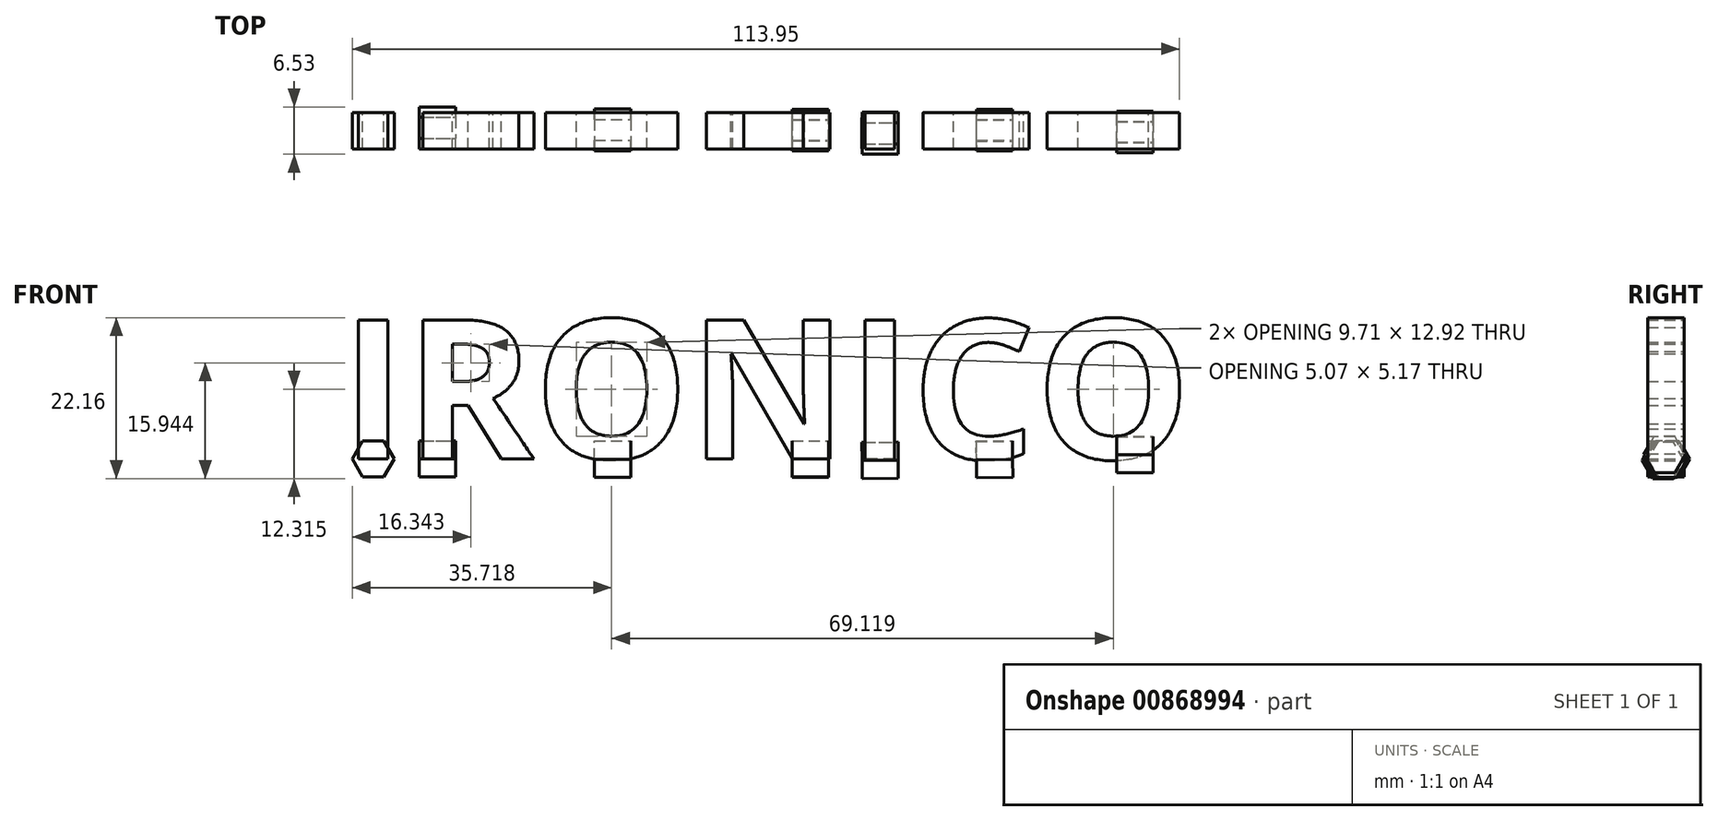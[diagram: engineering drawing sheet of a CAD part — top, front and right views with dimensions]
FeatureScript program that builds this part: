
annotation { "Feature Type Name" : "Feature", "Feature Type Description" : "" }
export const myFeature = defineFeature(function(context is Context, id is Id, definition is map)
    precondition{}
    {
        {
            var Q0;
            Q0=qCreatedBy(makeId("Front.planeOp"),FACE);
            var sketch = newSketch(context, id + "F0", { "sketchPlane" : qUnion([Q0])});
            skText(sketch, "E0", { "text": "IRONICO\n", "fontName": "OpenSans-Bold.ttf"});
            const initialGuessF0  = {"E0": [-0.04507, 0, 1, 0, 0.01931]};
            skSetInitialGuess(sketch, initialGuessF0);
            skSolve(sketch);
        }
        {
            var Q0;
            Q0 = qSketchRegion(id + "F0", true);
            extrude(context, id + "F1", {"entities" : qUnion([Q0]), "depth" : 5 * mm, "offsetDistance" : 25 * mm});
        }
        {
            var Q0;
            Q0=qCreatedBy(makeId("Front.planeOp"),FACE);
            var sketch = newSketch(context, id + "F2", { "sketchPlane" : qUnion([Q0])});
            skCircle(sketch, "E1.cCircle", {"center": v(-40.65, 0) * mm, "radius": 2.5 * mm, "construction": true});
            skLineSegment(sketch, "E1.0", {"start": v(-37.76, 0) * mm, "end": v(-39.2, -2.5) * mm});
            skLineSegment(sketch, "E1.1", {"start": v(-39.2, -2.5) * mm, "end": v(-42.09, -2.5) * mm});
            skLineSegment(sketch, "E1.2", {"start": v(-42.09, -2.5) * mm, "end": v(-43.53, 0) * mm});
            skLineSegment(sketch, "E1.3", {"start": v(-43.53, 0) * mm, "end": v(-42.09, 2.5) * mm});
            skLineSegment(sketch, "E1.4", {"start": v(-42.09, 2.5) * mm, "end": v(-39.2, 2.5) * mm});
            skLineSegment(sketch, "E1.5", {"start": v(-39.2, 2.5) * mm, "end": v(-37.76, 0) * mm});
            skPoint(sketch, "E1.0.midPoint", {"position": v(-38.48, -1.25) * mm});
            skCircle(sketch, "E2.cCircle", {"center": v(-31.74, 0) * mm, "radius": 2.5 * mm, "construction": true});
            skLineSegment(sketch, "E2.0", {"start": v(-28.85, 0) * mm, "end": v(-30.3, -2.5) * mm});
            skLineSegment(sketch, "E2.1", {"start": v(-30.3, -2.5) * mm, "end": v(-33.18, -2.5) * mm});
            skLineSegment(sketch, "E2.2", {"start": v(-33.18, -2.5) * mm, "end": v(-34.62, 0) * mm});
            skLineSegment(sketch, "E2.3", {"start": v(-34.62, 0) * mm, "end": v(-33.18, 2.5) * mm});
            skLineSegment(sketch, "E2.4", {"start": v(-33.18, 2.5) * mm, "end": v(-30.3, 2.5) * mm});
            skLineSegment(sketch, "E2.5", {"start": v(-30.3, 2.5) * mm, "end": v(-28.85, 0) * mm});
            skPoint(sketch, "E2.0.midPoint", {"position": v(-29.57, -1.25) * mm});
            skCircle(sketch, "E3.cCircle", {"center": v(-7.76, 0) * mm, "radius": 2.5 * mm, "construction": true});
            skLineSegment(sketch, "E3.0", {"start": v(-4.87, 0) * mm, "end": v(-6.31, -2.5) * mm});
            skLineSegment(sketch, "E3.1", {"start": v(-6.31, -2.5) * mm, "end": v(-9.2, -2.5) * mm});
            skLineSegment(sketch, "E3.2", {"start": v(-9.2, -2.5) * mm, "end": v(-10.64, 0) * mm});
            skLineSegment(sketch, "E3.3", {"start": v(-10.64, 0) * mm, "end": v(-9.2, 2.5) * mm});
            skLineSegment(sketch, "E3.4", {"start": v(-9.2, 2.5) * mm, "end": v(-6.31, 2.5) * mm});
            skLineSegment(sketch, "E3.5", {"start": v(-6.31, 2.5) * mm, "end": v(-4.87, 0) * mm});
            skPoint(sketch, "E3.0.midPoint", {"position": v(-5.6, -1.25) * mm});
            skCircle(sketch, "E4.cCircle", {"center": v(7.09, 0) * mm, "radius": 2.5 * mm, "construction": true});
            skLineSegment(sketch, "E4.0", {"start": v(9.98, 0.02) * mm, "end": v(8.55, -2.49) * mm});
            skLineSegment(sketch, "E4.1", {"start": v(8.55, -2.49) * mm, "end": v(5.66, -2.51) * mm});
            skLineSegment(sketch, "E4.2", {"start": v(5.66, -2.51) * mm, "end": v(4.2, -0.02) * mm});
            skLineSegment(sketch, "E4.3", {"start": v(4.2, -0.02) * mm, "end": v(5.63, 2.49) * mm});
            skLineSegment(sketch, "E4.4", {"start": v(5.63, 2.49) * mm, "end": v(8.51, 2.51) * mm});
            skLineSegment(sketch, "E4.5", {"start": v(8.51, 2.51) * mm, "end": v(9.98, 0.02) * mm});
            skPoint(sketch, "E4.0.midPoint", {"position": v(9.26, -1.23) * mm});
            skCircle(sketch, "E5.cCircle", {"center": v(29.25, 0) * mm, "radius": 2.5 * mm, "construction": true});
            skLineSegment(sketch, "E5.0", {"start": v(32.14, 0.02) * mm, "end": v(30.72, -2.49) * mm});
            skLineSegment(sketch, "E5.1", {"start": v(30.72, -2.49) * mm, "end": v(27.83, -2.51) * mm});
            skLineSegment(sketch, "E5.2", {"start": v(27.83, -2.51) * mm, "end": v(26.37, -0.02) * mm});
            skLineSegment(sketch, "E5.3", {"start": v(26.37, -0.02) * mm, "end": v(27.8, 2.49) * mm});
            skLineSegment(sketch, "E5.4", {"start": v(27.8, 2.49) * mm, "end": v(30.68, 2.51) * mm});
            skLineSegment(sketch, "E5.5", {"start": v(30.68, 2.51) * mm, "end": v(32.14, 0.02) * mm});
            skPoint(sketch, "E5.0.midPoint", {"position": v(31.43, -1.23) * mm});
            skCircle(sketch, "E6.cCircle", {"center": v(44.36, -0.36) * mm, "radius": 2.5 * mm, "construction": true});
            skLineSegment(sketch, "E6.0", {"start": v(47.24, -0.4) * mm, "end": v(45.77, -2.88) * mm});
            skLineSegment(sketch, "E6.1", {"start": v(45.77, -2.88) * mm, "end": v(42.88, -2.85) * mm});
            skLineSegment(sketch, "E6.2", {"start": v(42.88, -2.85) * mm, "end": v(41.47, -0.33) * mm});
            skLineSegment(sketch, "E6.3", {"start": v(41.47, -0.33) * mm, "end": v(42.94, 2.15) * mm});
            skLineSegment(sketch, "E6.4", {"start": v(42.94, 2.15) * mm, "end": v(45.83, 2.12) * mm});
            skLineSegment(sketch, "E6.5", {"start": v(45.83, 2.12) * mm, "end": v(47.24, -0.4) * mm});
            skPoint(sketch, "E6.0.midPoint", {"position": v(46.5, -1.64) * mm});
            skCircle(sketch, "E7.cCircle", {"center": v(61.76, 0) * mm, "radius": 2.5 * mm, "construction": true});
            skLineSegment(sketch, "E7.0", {"start": v(64.65, -0.03) * mm, "end": v(63.18, -2.51) * mm});
            skLineSegment(sketch, "E7.1", {"start": v(63.18, -2.51) * mm, "end": v(60.3, -2.49) * mm});
            skLineSegment(sketch, "E7.2", {"start": v(60.3, -2.49) * mm, "end": v(58.88, 0.03) * mm});
            skLineSegment(sketch, "E7.3", {"start": v(58.88, 0.03) * mm, "end": v(60.34, 2.51) * mm});
            skLineSegment(sketch, "E7.4", {"start": v(60.34, 2.51) * mm, "end": v(63.23, 2.49) * mm});
            skLineSegment(sketch, "E7.5", {"start": v(63.23, 2.49) * mm, "end": v(64.65, -0.03) * mm});
            skPoint(sketch, "E7.0.midPoint", {"position": v(63.92, -1.27) * mm});
            skLineSegment(sketch, "E8", {"start": v(-40.65, 2.5) * mm, "end": v(-40.65, -2.5) * mm});
            skLineSegment(sketch, "E9", {"start": v(-31.74, 2.5) * mm, "end": v(-31.74, -2.5) * mm});
            skLineSegment(sketch, "E10", {"start": v(-7.76, 2.5) * mm, "end": v(-7.76, -2.5) * mm});
            skLineSegment(sketch, "E11", {"start": v(7.07, 2.5) * mm, "end": v(7.07, -2.5) * mm});
            skLineSegment(sketch, "E12", {"start": v(29.24, 2.5) * mm, "end": v(29.25, -2.5) * mm});
            skLineSegment(sketch, "E13", {"start": v(44.39, 2.14) * mm, "end": v(44.42, -2.87) * mm});
            skLineSegment(sketch, "E14", {"start": v(61.79, 2.5) * mm, "end": v(61.79, -2.5) * mm});
            skSolve(sketch);
        }
        {
            var Q0;
            Q0 = qSketchRegion(id + "F2", true);
            extrude(context, id + "F3", {"entities" : qUnion([Q0]), "depth" : 5 * mm, "offsetDistance" : 25 * mm});
        }
        {
            var Q0;
            Q0=makeQuery(id+"F3.opExtrude","SWEPT_BODY",BODY,{"disambiguationData":[OSD([sQuery(id+"F2.wireOp",EDGE,"E1.0"),sQuery(id+"F2.wireOp",EDGE,"E1.1"),sQuery(id+"F2.wireOp",EDGE,"E1.2"),sQuery(id+"F2.wireOp",EDGE,"E1.3"),sQuery(id+"F2.wireOp",EDGE,"E1.4"),sQuery(id+"F2.wireOp",EDGE,"E1.5")])]});
            transform(context, id + "F4", {"entities" : qUnion([Q0]), "transformType" : TransformType.TRANSLATION_3D, "dx" : -2.8 * mm, "dy" : 2.6 * mm, "dz" : 0 * mm, "makeCopy" : false});
        }
        {
            var Q0;
            Q0=makeQuery(id+"F3.opExtrude","SWEPT_BODY",BODY,{"disambiguationData":[OSD([sQuery(id+"F2.wireOp",EDGE,"E1.0"),sQuery(id+"F2.wireOp",EDGE,"E1.1"),sQuery(id+"F2.wireOp",EDGE,"E1.2"),sQuery(id+"F2.wireOp",EDGE,"E1.3"),sQuery(id+"F2.wireOp",EDGE,"E1.4"),sQuery(id+"F2.wireOp",EDGE,"E1.5")])]});
            transform(context, id + "F5", {"entities" : qUnion([Q0]), "transformType" : TransformType.TRANSLATION_3D, "dx" : 2.8 * mm, "dy" : -2.6 * mm, "dz" : 0 * mm, "makeCopy" : false});
        }
        {
            var Q0;
            Q0=sQuery(id+"F2.wireOp",EDGE,"E14");
            var Q1;
            Q1=sQuery(id+"F2.wireOp",EDGE,"E13");
            var Q2;
            Q2=sQuery(id+"F2.wireOp",EDGE,"E12");
            var Q3;
            Q3=sQuery(id+"F2.wireOp",EDGE,"E11");
            var Q4;
            Q4=sQuery(id+"F2.wireOp",EDGE,"E8");
            var Q5;
            Q5=sQuery(id+"F2.wireOp",EDGE,"E9");
            var Q6;
            Q6=sQuery(id+"F2.wireOp",EDGE,"E10");
            extrude(context, id + "F6", {"bodyType" : ToolBodyType.SURFACE, "surfaceEntities" : qUnion([Q0, Q1, Q2, Q3, Q4, Q5, Q6]), "depth" : 5 * mm, "offsetDistance" : 25 * mm});
        }
        {
            var Q0;
            Q0=makeQuery(id+"F3.opExtrude","SWEPT_BODY",BODY,{"disambiguationData":[OSD([sQuery(id+"F2.wireOp",EDGE,"E2.0"),sQuery(id+"F2.wireOp",EDGE,"E2.1"),sQuery(id+"F2.wireOp",EDGE,"E2.2"),sQuery(id+"F2.wireOp",EDGE,"E2.3"),sQuery(id+"F2.wireOp",EDGE,"E2.4"),sQuery(id+"F2.wireOp",EDGE,"E2.5")])]});
            var Q1;
            Q1=makeQuery(id+"F6.opExtrude","SWEPT_BODY",BODY,{"disambiguationData":[OSD([sQuery(id+"F2.wireOp",EDGE,"E9")])]});
            var Q2;
            Q2=makeQuery(id+"F6.opExtrude","CAP_EDGE",EDGE,{"disambiguationData":[OSD([sQuery(id+"F2.wireOp",EDGE,"E9")])],"isStart":true});
            transform(context, id + "F7", {"entities" : qUnion([Q0, Q1]), "transformType" : TransformType.ROTATION, "transformAxis" : qUnion([Q2]), "angle" : 90 * degree, "makeCopy" : false});
        }
        {
            var Q0;
            Q0=makeQuery(id+"F3.opExtrude","SWEPT_BODY",BODY,{"disambiguationData":[OSD([sQuery(id+"F2.wireOp",EDGE,"E2.0"),sQuery(id+"F2.wireOp",EDGE,"E2.1"),sQuery(id+"F2.wireOp",EDGE,"E2.2"),sQuery(id+"F2.wireOp",EDGE,"E2.3"),sQuery(id+"F2.wireOp",EDGE,"E2.4"),sQuery(id+"F2.wireOp",EDGE,"E2.5")])]});
            var Q1;
            Q1=makeQuery(id+"F6.opExtrude","SWEPT_BODY",BODY,{"disambiguationData":[OSD([sQuery(id+"F2.wireOp",EDGE,"E9")])]});
            transform(context, id + "F8", {"entities" : qUnion([Q0, Q1]), "transformType" : TransformType.TRANSLATION_3D, "dx" : 2.44 * mm, "dy" : -2.1 * mm, "dz" : 0 * mm, "makeCopy" : false});
        }
        {
            var Q0;
            Q0=makeQuery(id+"F3.opExtrude","SWEPT_BODY",BODY,{"disambiguationData":[OSD([sQuery(id+"F2.wireOp",EDGE,"E3.0"),sQuery(id+"F2.wireOp",EDGE,"E3.1"),sQuery(id+"F2.wireOp",EDGE,"E3.2"),sQuery(id+"F2.wireOp",EDGE,"E3.3"),sQuery(id+"F2.wireOp",EDGE,"E3.4"),sQuery(id+"F2.wireOp",EDGE,"E3.5")])]});
            var Q1;
            Q1=makeQuery(id+"F6.opExtrude","SWEPT_BODY",BODY,{"disambiguationData":[OSD([sQuery(id+"F2.wireOp",EDGE,"E10")])]});
            var Q2;
            Q2=makeQuery(id+"F6.opExtrude","CAP_EDGE",EDGE,{"disambiguationData":[OSD([sQuery(id+"F2.wireOp",EDGE,"E10")])],"isStart":false});
            transform(context, id + "F9", {"entities" : qUnion([Q0, Q1]), "transformType" : TransformType.ROTATION, "transformAxis" : qUnion([Q2]), "angle" : 90 * degree, "makeCopy" : false});
        }
        {
            var Q0;
            Q0=makeQuery(id+"F3.opExtrude","SWEPT_BODY",BODY,{"disambiguationData":[OSD([sQuery(id+"F2.wireOp",EDGE,"E3.0"),sQuery(id+"F2.wireOp",EDGE,"E3.1"),sQuery(id+"F2.wireOp",EDGE,"E3.2"),sQuery(id+"F2.wireOp",EDGE,"E3.3"),sQuery(id+"F2.wireOp",EDGE,"E3.4"),sQuery(id+"F2.wireOp",EDGE,"E3.5")])]});
            var Q1;
            Q1=makeQuery(id+"F6.opExtrude","SWEPT_BODY",BODY,{"disambiguationData":[OSD([sQuery(id+"F2.wireOp",EDGE,"E10")])]});
            transform(context, id + "F10", {"entities" : qUnion([Q0, Q1]), "transformType" : TransformType.TRANSLATION_3D, "dx" : -2.4 * mm, "dy" : 2.6 * mm, "dz" : -0.05 * mm, "makeCopy" : false});
        }
        {
            var Q0;
            Q0=makeQuery(id+"F3.opExtrude","SWEPT_BODY",BODY,{"disambiguationData":[OSD([sQuery(id+"F2.wireOp",EDGE,"E4.0"),sQuery(id+"F2.wireOp",EDGE,"E4.1"),sQuery(id+"F2.wireOp",EDGE,"E4.2"),sQuery(id+"F2.wireOp",EDGE,"E4.3"),sQuery(id+"F2.wireOp",EDGE,"E4.4"),sQuery(id+"F2.wireOp",EDGE,"E4.5")])]});
            var Q1;
            Q1=makeQuery(id+"F6.opExtrude","SWEPT_BODY",BODY,{"disambiguationData":[OSD([sQuery(id+"F2.wireOp",EDGE,"E11")])]});
            var Q2;
            Q2=makeQuery(id+"F6.opExtrude","CAP_EDGE",EDGE,{"disambiguationData":[OSD([sQuery(id+"F2.wireOp",EDGE,"E11")])],"isStart":true});
            transform(context, id + "F11", {"entities" : qUnion([Q0, Q1]), "transformType" : TransformType.ROTATION, "transformAxis" : qUnion([Q2]), "angle" : 90 * degree, "makeCopy" : false});
        }
        {
            var Q0;
            Q0=makeQuery(id+"F3.opExtrude","SWEPT_BODY",BODY,{"disambiguationData":[OSD([sQuery(id+"F2.wireOp",EDGE,"E4.0"),sQuery(id+"F2.wireOp",EDGE,"E4.1"),sQuery(id+"F2.wireOp",EDGE,"E4.2"),sQuery(id+"F2.wireOp",EDGE,"E4.3"),sQuery(id+"F2.wireOp",EDGE,"E4.4"),sQuery(id+"F2.wireOp",EDGE,"E4.5")])]});
            var Q1;
            Q1=makeQuery(id+"F6.opExtrude","SWEPT_BODY",BODY,{"disambiguationData":[OSD([sQuery(id+"F2.wireOp",EDGE,"E11")])]});
            transform(context, id + "F12", {"entities" : qUnion([Q0, Q1]), "transformType" : TransformType.TRANSLATION_3D, "dx" : 15 * mm, "dy" : -2.4 * mm, "dz" : 0 * mm, "makeCopy" : false});
        }
        {
            var Q0;
            Q0=makeQuery(id+"F3.opExtrude","SWEPT_BODY",BODY,{"disambiguationData":[OSD([sQuery(id+"F2.wireOp",EDGE,"E5.0"),sQuery(id+"F2.wireOp",EDGE,"E5.1"),sQuery(id+"F2.wireOp",EDGE,"E5.2"),sQuery(id+"F2.wireOp",EDGE,"E5.3"),sQuery(id+"F2.wireOp",EDGE,"E5.4"),sQuery(id+"F2.wireOp",EDGE,"E5.5")])]});
            var Q1;
            Q1=makeQuery(id+"F6.opExtrude","SWEPT_BODY",BODY,{"disambiguationData":[OSD([sQuery(id+"F2.wireOp",EDGE,"E12")])]});
            var Q2;
            Q2=makeQuery(id+"F6.opExtrude","CAP_EDGE",EDGE,{"disambiguationData":[OSD([sQuery(id+"F2.wireOp",EDGE,"E12")])],"isStart":false});
            transform(context, id + "F13", {"entities" : qUnion([Q0, Q1]), "transformType" : TransformType.ROTATION, "transformAxis" : qUnion([Q2]), "angle" : 90 * degree, "makeCopy" : false});
        }
        {
            var Q0;
            Q0=makeQuery(id+"F6.opExtrude","SWEPT_BODY",BODY,{"disambiguationData":[OSD([sQuery(id+"F2.wireOp",EDGE,"E12")])]});
            var Q1;
            Q1=makeQuery(id+"F3.opExtrude","SWEPT_BODY",BODY,{"disambiguationData":[OSD([sQuery(id+"F2.wireOp",EDGE,"E5.0"),sQuery(id+"F2.wireOp",EDGE,"E5.1"),sQuery(id+"F2.wireOp",EDGE,"E5.2"),sQuery(id+"F2.wireOp",EDGE,"E5.3"),sQuery(id+"F2.wireOp",EDGE,"E5.4"),sQuery(id+"F2.wireOp",EDGE,"E5.5")])]});
            transform(context, id + "F14", {"entities" : qUnion([Q0, Q1]), "transformType" : TransformType.TRANSLATION_3D, "dx" : -2.55 * mm, "dy" : 2.15 * mm, "dz" : -0.2 * mm, "makeCopy" : false});
        }
        {
            var Q0;
            Q0=makeQuery(id+"F3.opExtrude","SWEPT_BODY",BODY,{"disambiguationData":[OSD([sQuery(id+"F2.wireOp",EDGE,"E6.0"),sQuery(id+"F2.wireOp",EDGE,"E6.1"),sQuery(id+"F2.wireOp",EDGE,"E6.2"),sQuery(id+"F2.wireOp",EDGE,"E6.3"),sQuery(id+"F2.wireOp",EDGE,"E6.4"),sQuery(id+"F2.wireOp",EDGE,"E6.5")])]});
            var Q1;
            Q1=makeQuery(id+"F6.opExtrude","SWEPT_BODY",BODY,{"disambiguationData":[OSD([sQuery(id+"F2.wireOp",EDGE,"E13")])]});
            var Q2;
            Q2=makeQuery(id+"F6.opExtrude","CAP_EDGE",EDGE,{"disambiguationData":[OSD([sQuery(id+"F2.wireOp",EDGE,"E13")])],"isStart":false});
            transform(context, id + "F15", {"entities" : qUnion([Q0, Q1]), "transformType" : TransformType.ROTATION, "transformAxis" : qUnion([Q2]), "angle" : 90 * degree, "makeCopy" : false});
        }
        {
            var Q0;
            Q0=makeQuery(id+"F3.opExtrude","SWEPT_BODY",BODY,{"disambiguationData":[OSD([sQuery(id+"F2.wireOp",EDGE,"E6.0"),sQuery(id+"F2.wireOp",EDGE,"E6.1"),sQuery(id+"F2.wireOp",EDGE,"E6.2"),sQuery(id+"F2.wireOp",EDGE,"E6.3"),sQuery(id+"F2.wireOp",EDGE,"E6.4"),sQuery(id+"F2.wireOp",EDGE,"E6.5")])]});
            var Q1;
            Q1=makeQuery(id+"F6.opExtrude","SWEPT_BODY",BODY,{"disambiguationData":[OSD([sQuery(id+"F2.wireOp",EDGE,"E13")])]});
            transform(context, id + "F16", {"entities" : qUnion([Q0, Q1]), "transformType" : TransformType.TRANSLATION_3D, "dx" : -1.96 * mm, "dy" : 2.53 * mm, "dz" : 0.31 * mm, "makeCopy" : false});
        }
        {
            var Q0;
            Q0=makeQuery(id+"F3.opExtrude","SWEPT_BODY",BODY,{"disambiguationData":[OSD([sQuery(id+"F2.wireOp",EDGE,"E7.0"),sQuery(id+"F2.wireOp",EDGE,"E7.1"),sQuery(id+"F2.wireOp",EDGE,"E7.2"),sQuery(id+"F2.wireOp",EDGE,"E7.3"),sQuery(id+"F2.wireOp",EDGE,"E7.4"),sQuery(id+"F2.wireOp",EDGE,"E7.5")])]});
            var Q1;
            Q1=makeQuery(id+"F6.opExtrude","SWEPT_BODY",BODY,{"disambiguationData":[OSD([sQuery(id+"F2.wireOp",EDGE,"E14")])]});
            var Q2;
            Q2=makeQuery(id+"F6.opExtrude","CAP_EDGE",EDGE,{"disambiguationData":[OSD([sQuery(id+"F2.wireOp",EDGE,"E14")])],"isStart":false});
            transform(context, id + "F17", {"entities" : qUnion([Q0, Q1]), "transformType" : TransformType.ROTATION, "transformAxis" : qUnion([Q2]), "angle" : 90 * degree, "makeCopy" : false});
        }
        {
            var Q0;
            Q0=makeQuery(id+"F3.opExtrude","SWEPT_BODY",BODY,{"disambiguationData":[OSD([sQuery(id+"F2.wireOp",EDGE,"E7.0"),sQuery(id+"F2.wireOp",EDGE,"E7.1"),sQuery(id+"F2.wireOp",EDGE,"E7.2"),sQuery(id+"F2.wireOp",EDGE,"E7.3"),sQuery(id+"F2.wireOp",EDGE,"E7.4"),sQuery(id+"F2.wireOp",EDGE,"E7.5")])]});
            var Q1;
            Q1=makeQuery(id+"F6.opExtrude","SWEPT_BODY",BODY,{"disambiguationData":[OSD([sQuery(id+"F2.wireOp",EDGE,"E14")])]});
            transform(context, id + "F18", {"entities" : qUnion([Q0, Q1]), "transformType" : TransformType.TRANSLATION_3D, "dx" : 0 * mm, "dy" : 2.3 * mm, "dz" : 0.6 * mm, "makeCopy" : false});
        }
    });
